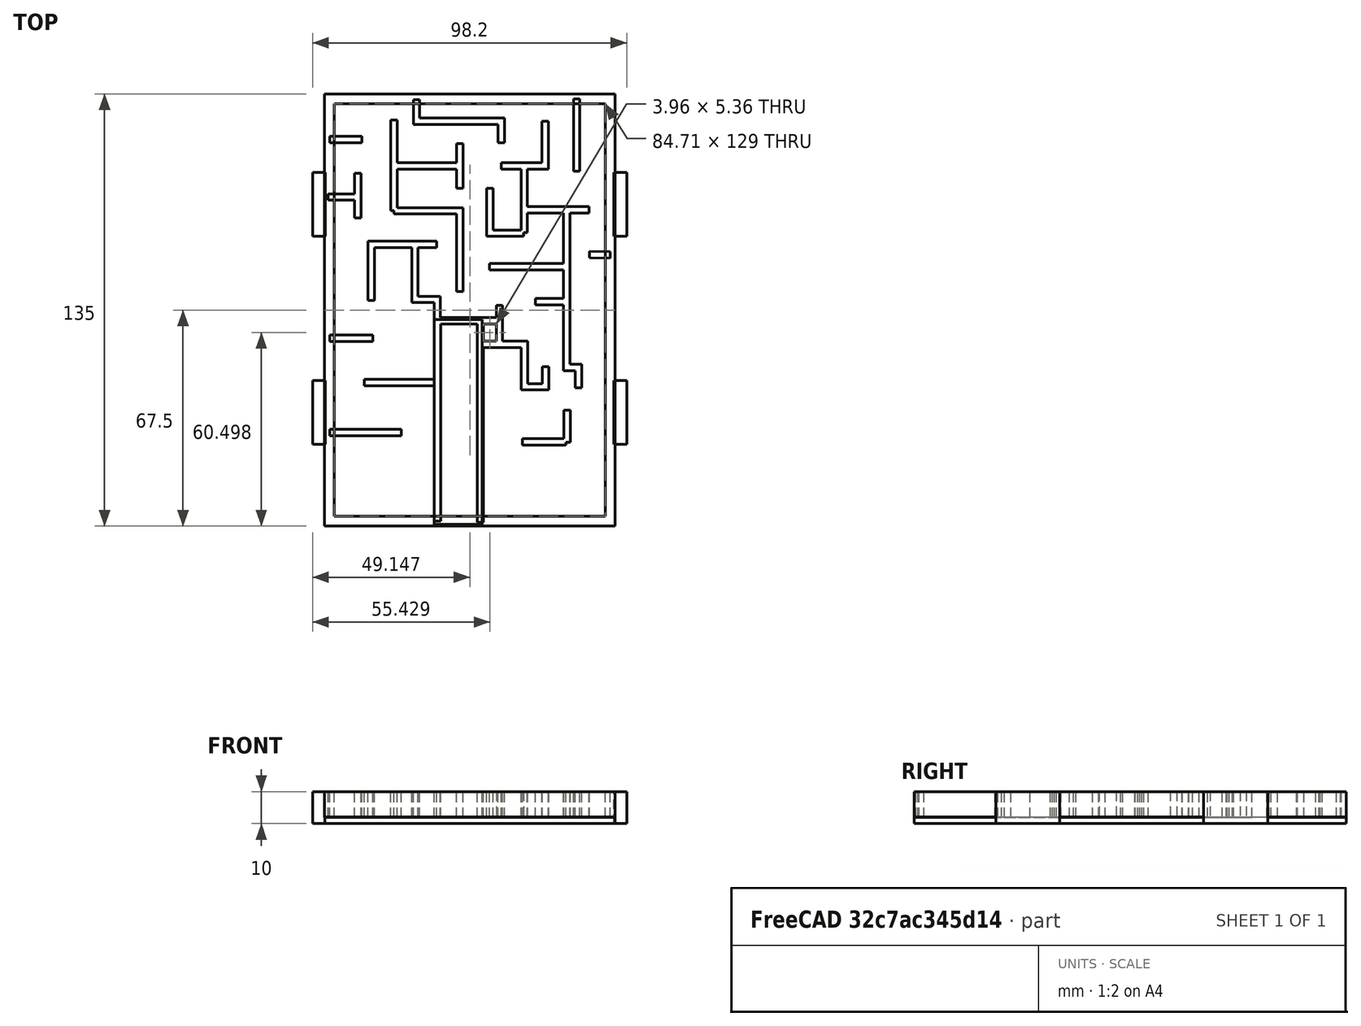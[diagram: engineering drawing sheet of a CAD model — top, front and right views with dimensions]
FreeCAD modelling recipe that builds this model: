
FCSTD DOCUMENT  (FreeCAD 0.16R)
Label: labyrinth2
License: All rights reserved
LicenseURL: http://en.wikipedia.org/wiki/All_rights_reserved
objects: Part::Box×6, Sketcher::SketchObject×3, Part::FeaturePython×2
note: 11 computed .brp shape members not serialized (recipe doc carries the construction recipe); baked Part::Feature solids carry a one-line shape summary decoded from their .brp

FEATURE [Sketcher::SketchObject] Sketch  label="Border"
  sketch-geometry (4):
    g0: LineSegment StartX=1.29414 StartY=-2 StartZ=0 EndX=89 EndY=-2 EndZ=0
    g1: LineSegment StartX=89 StartY=-2 StartZ=0 EndX=89 EndY=-134 EndZ=0
    g2: LineSegment StartX=89 StartY=-134 StartZ=0 EndX=1.29414 EndY=-134 EndZ=0
    g3: LineSegment StartX=1.29414 StartY=-134 StartZ=0 EndX=1.29414 EndY=-2 EndZ=0
  constraints (5):
    c: Horizontal(g0)
    c: Vertical(g1)
    c: Horizontal(g2)
    c: Coincident(g3,g0)
    c: Vertical(g3)
FEATURE [Sketcher::SketchObject] Sketch001  label="Labyrinth"
  sketch-geometry (42):
    g0: LineSegment StartX=1.43476 StartY=-14.7187 StartZ=0 EndX=11.4126 EndY=-14.7187 EndZ=0
    g1: LineSegment StartX=28.5085 StartY=-2.21682 StartZ=0 EndX=28.5085 EndY=-9 EndZ=0
    g2: LineSegment StartX=28.5085 StartY=-9 StartZ=0 EndX=55 EndY=-9 EndZ=0
    g3: LineSegment StartX=55 StartY=-9 StartZ=0 EndX=55 EndY=-15.7278 EndZ=0
    g4: LineSegment StartX=68.6824 StartY=-9 StartZ=0 EndX=68.6824 EndY=-22.9293 EndZ=0
    g5: LineSegment StartX=68.6824 StartY=-22.9293 StartZ=0 EndX=55 EndY=-22.9293 EndZ=0
    g6: LineSegment StartX=62.1633 StartY=-22.9293 StartZ=0 EndX=62.1633 EndY=-43.7732 EndZ=0
    g7: LineSegment StartX=62 StartY=-44 StartZ=0 EndX=51.4715 EndY=-44 EndZ=0
    g8: LineSegment StartX=51.4715 StartY=-44 StartZ=0 EndX=51.4715 EndY=-30 EndZ=0
    g9: LineSegment StartX=42 StartY=-16 StartZ=0 EndX=42 EndY=-30 EndZ=0
    g10: LineSegment StartX=42 StartY=-23 StartZ=0 EndX=21.4988 EndY=-23 EndZ=0
    g11: LineSegment StartX=21.4988 StartY=-8.66521 StartZ=0 EndX=21.4988 EndY=-37 EndZ=0
    g12: LineSegment StartX=21.4965 StartY=-37 StartZ=0 EndX=42 EndY=-37 EndZ=0
    g13: LineSegment StartX=42 StartY=-37 StartZ=0 EndX=42 EndY=-62.2722 EndZ=0
    g14: LineSegment StartX=51.2622 StartY=-54.4956 StartZ=0 EndX=75.4132 EndY=-54.4956 EndZ=0
    g15: LineSegment StartX=75.4132 StartY=-86 StartZ=0 EndX=75.4132 EndY=-36.679 EndZ=0
    g16: LineSegment StartX=62.1633 StartY=-36.679 StartZ=0 EndX=82.3981 EndY=-36.679 EndZ=0
    g17: LineSegment StartX=78.5506 StartY=-24.6654 StartZ=0 EndX=78.5506 EndY=-2 EndZ=0
    g18: LineSegment StartX=89 StartY=-50.7334 StartZ=0 EndX=82.5128 EndY=-50.6705 EndZ=0
    g19: LineSegment StartX=79.1291 StartY=-86 StartZ=0 EndX=79.1291 EndY=-92.3402 EndZ=0
    g20: LineSegment StartX=75.4132 StartY=-65.4042 StartZ=0 EndX=65.637 EndY=-65.4042 EndZ=0
    g21: LineSegment StartX=75.4132 StartY=-86 StartZ=0 EndX=79.1291 EndY=-86 EndZ=0
    g22: LineSegment StartX=14.7944 StartY=-76.8211 StartZ=0 EndX=1.43698 EndY=-76.8211 EndZ=0
    g23: LineSegment StartX=54.4082 StartY=-66.5797 StartZ=0 EndX=54.4082 EndY=-78.6801 EndZ=0
    g24: LineSegment StartX=54.4082 StartY=-71.325 StartZ=0 EndX=34.9882 EndY=-71.325 EndZ=0
    g25: LineSegment StartX=34.7383 StartY=-47.4326 StartZ=0 EndX=14.3489 EndY=-47.4326 EndZ=0
    g26: LineSegment StartX=0.898084 StartY=-32.6862 StartZ=0 EndX=10.142 EndY=-32.6862 EndZ=0
    g27: LineSegment StartX=10.142 StartY=-25.2353 StartZ=0 EndX=10.142 EndY=-39.2353 EndZ=0
    g28: LineSegment StartX=14.3489 StartY=-47.4326 StartZ=0 EndX=14.3489 EndY=-65 EndZ=0
    g29: LineSegment StartX=28 StartY=-64.6816 StartZ=0 EndX=34.9882 EndY=-64.6816 EndZ=0
    g30: LineSegment StartX=34.9882 StartY=-64.6816 StartZ=0 EndX=34.9882 EndY=-71.325 EndZ=0
    g31: LineSegment StartX=35.0707 StartY=-71.4106 StartZ=0 EndX=35.0707 EndY=-134 EndZ=0
    g32: LineSegment StartX=12.1552 StartY=-90.6611 StartZ=0 EndX=34.7888 EndY=-90.6611 EndZ=0
    g33: LineSegment StartX=23.7896 StartY=-106.258 StartZ=0 EndX=1.4345 EndY=-106.258 EndZ=0
    g34: LineSegment StartX=48.4506 StartY=-134.345 StartZ=0 EndX=48.4506 EndY=-72 EndZ=0
    g35: LineSegment StartX=75.5914 StartY=-99.287 StartZ=0 EndX=75.5914 EndY=-109.304 EndZ=0
    g36: LineSegment StartX=61.5805 StartY=-109.189 StartZ=0 EndX=75.2229 EndY=-109.189 EndZ=0
    g37: LineSegment StartX=48.7717 StartY=-78.6801 StartZ=0 EndX=62.236 EndY=-78.6801 EndZ=0
    g38: LineSegment StartX=62.236 StartY=-78.6801 StartZ=0 EndX=62.236 EndY=-92 EndZ=0
    g39: LineSegment StartX=62.236 StartY=-92 StartZ=0 EndX=68.7845 EndY=-92 EndZ=0
    g40: LineSegment StartX=68.7845 StartY=-92 StartZ=0 EndX=68.7845 EndY=-85.6777 EndZ=0
    g41: LineSegment StartX=28 StartY=-64.6816 StartZ=0 EndX=28 EndY=-47.4326 EndZ=0
  constraints (64):
    c: Horizontal(g0)
    c: Vertical(g1)
    c: Horizontal(g2)
    c: Vertical(g3)
    c: Vertical(g4)
    c: Horizontal(g5)
    c: Vertical(g6)
    c: Horizontal(g7)
    c: Vertical(g8)
    c: Vertical(g9)
    c: PointOnObject(g10,g9)
    c: Horizontal(g10)
    c: Vertical(g11)
    c: Horizontal(g12)
    c: Vertical(g13)
    c: Horizontal(g14)
    c: PointOnObject(g16,g6)
    c: Horizontal(g16)
    c: Vertical(g17)
    c: Vertical(g19)
    c: Horizontal(g20)
    c: Horizontal(g21)
    c: Horizontal(g22)
    c: Vertical(g23)
    c: PointOnObject(g24,g23)
    c: Horizontal(g24)
    c: Horizontal(g25)
    c: Horizontal(g26)
    c: Vertical(g27)
    c: PointOnObject(g28,g25)
    c: Vertical(g28)
    c: Horizontal(g29)
    c: Coincident(g30,g24)
    c: Vertical(g30)
    c: Vertical(g31)
    c: Horizontal(g32)
    c: Horizontal(g33)
    c: Vertical(g34)
    c: Vertical(g35)
    c: Horizontal(g36)
    c: Horizontal(g37)
    c: Vertical(g38)
    c: Horizontal(g39)
    c: Vertical(g40)
    c: PointOnObject(g41,g25)
    c: Vertical(g41)
    c: Perpendicular(g14,g15) = 1.5708
    c: PointOnObject(g20,g15)
    c: PointOnObject(g15,g16)
    c: Coincident(g4,g5)
    c: PointOnObject(g6,g5)
    c: Coincident(g2,g3)
    c: Coincident(g1,g2)
    c: PointOnObject(g10,g11)
    c: PointOnObject(g26,g27)
    c: Coincident(g29,g41)
    c: Coincident(g29,g30)
    c: Coincident(g25,g28)
    c: PointOnObject(g23,g37)
    c: Coincident(g37,g38)
    c: Coincident(g38,g39)
    c: Coincident(g39,g40)
    c: Coincident(g19,g21)
    c: Coincident(g15,g21)
FEATURE [Part::FeaturePython] Wall  label="LabyrinthWalls"  # WARN: FeaturePython — macro-defined, semantics opaque (R4)
  Align = 2
  Base = -> Sketch001
  Face = 0
  Height = 8
  Length = 744.465
  MoveWithHost = false
  Normal = (0,0,0)
  Role = 0
  Width = 2
FEATURE [Part::FeaturePython] Wall001  label="BorderWalls"  # WARN: FeaturePython — macro-defined, semantics opaque (R4)
  Align = 2
  Base = -> Sketch
  Face = 0
  Height = 8
  Length = 439.412
  MoveWithHost = false
  Normal = (0,0,0)
  Role = 0
  Width = 3
FEATURE [Part::Box] Box  label="Boden"
  Height = 2.1
  Length = 90.7
  Placement = pos=(-0.2,-135.5,-2) rot=(0,0,1;0rad)
  Width = 135
FEATURE [Part::Box] Box001  label="Cube"
  Height = 10
  Length = 4
  Placement = pos=(-4,-45,-2) rot=(0,0,1;0rad)
  Width = 20
FEATURE [Part::Box] Box003  label="Cube001"
  Height = 10
  Length = 4
  Placement = pos=(-4,-110,-2) rot=(0,0,1;0rad)
  Width = 20
FEATURE [Part::Box] Box004  label="Cube002"
  Height = 10
  Length = 4
  Placement = pos=(90.2,-110,-2) rot=(0,0,1;0rad)
  Width = 20
FEATURE [Part::Box] Box005  label="Cube003"
  Height = 10
  Length = 4
  Placement = pos=(90.2,-45,-2) rot=(0,0,1;0rad)
  Width = 20
FEATURE [Sketcher::SketchObject] Sketch002  label="Cover"
  sketch-geometry (20):
    g0: LineSegment StartX=90.2 StartY=-45 StartZ=0 EndX=90.2 EndY=-25 EndZ=0
    g1: LineSegment StartX=94.2 StartY=-45 StartZ=0 EndX=94.2 EndY=-25 EndZ=0
    g2: LineSegment StartX=90.2 StartY=-45 StartZ=0 EndX=94.2 EndY=-45 EndZ=0
    g3: LineSegment StartX=90.2 StartY=-25 StartZ=0 EndX=94.2 EndY=-25 EndZ=0
    g4: LineSegment StartX=90.2 StartY=-110 StartZ=0 EndX=90.2 EndY=-90 EndZ=0
    g5: LineSegment StartX=94.2 StartY=-110 StartZ=0 EndX=94.2 EndY=-90 EndZ=0
    g6: LineSegment StartX=90.2 StartY=-110 StartZ=0 EndX=94.2 EndY=-110 EndZ=0
    g7: LineSegment StartX=90.2 StartY=-90 StartZ=0 EndX=94.2 EndY=-90 EndZ=0
    g8: LineSegment StartX=-0.2 StartY=-135.5 StartZ=0 EndX=-0.2 EndY=-0.5 EndZ=0
    g9: LineSegment StartX=90.5 StartY=-135.5 StartZ=0 EndX=90.5 EndY=-0.5 EndZ=0
    g10: LineSegment StartX=-0.2 StartY=-135.5 StartZ=0 EndX=90.5 EndY=-135.5 EndZ=0
    g11: LineSegment StartX=-0.2 StartY=-0.5 StartZ=0 EndX=90.5 EndY=-0.5 EndZ=0
    g12: LineSegment StartX=-4 StartY=-110 StartZ=0 EndX=-4 EndY=-90 EndZ=0
    g13: LineSegment StartX=0 StartY=-110 StartZ=0 EndX=0 EndY=-90 EndZ=0
    g14: LineSegment StartX=-4 StartY=-110 StartZ=0 EndX=0 EndY=-110 EndZ=0
    g15: LineSegment StartX=-4 StartY=-90 StartZ=0 EndX=0 EndY=-90 EndZ=0
    g16: LineSegment StartX=-4 StartY=-45 StartZ=0 EndX=-4 EndY=-25 EndZ=0
    g17: LineSegment StartX=0 StartY=-45 StartZ=0 EndX=0 EndY=-25 EndZ=0
    g18: LineSegment StartX=-4 StartY=-45 StartZ=0 EndX=0 EndY=-45 EndZ=0
    g19: LineSegment StartX=-4 StartY=-25 StartZ=0 EndX=0 EndY=-25 EndZ=0
FEATURE [Part::Box] Box006  label="Cube004"
  Height = 8
  Length = 15
  Placement = pos=(34,-135,0) rot=(0,0,1;0rad)
  Width = 64
